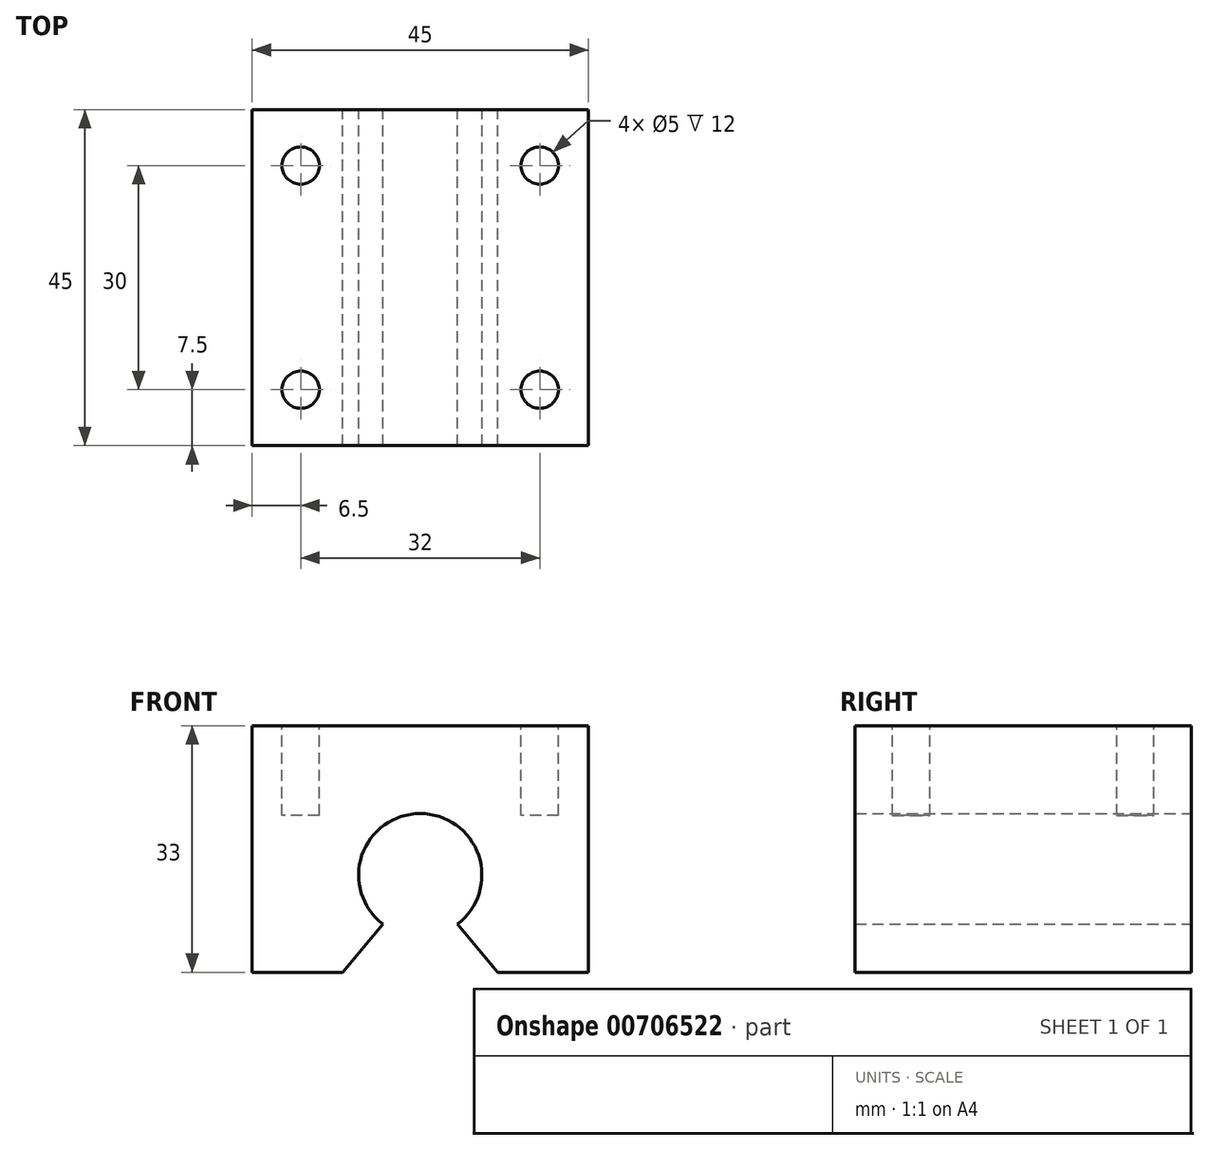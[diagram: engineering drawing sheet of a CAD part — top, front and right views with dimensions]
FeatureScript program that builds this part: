
annotation { "Feature Type Name" : "Feature", "Feature Type Description" : "" }
export const myFeature = defineFeature(function(context is Context, id is Id, definition is map)
    precondition{}
    {
        {
            var Q0;
            Q0=qCreatedBy(makeId("Front.planeOp"),FACE);
            var sketch = newSketch(context, id + "F0", { "sketchPlane" : qUnion([Q0])});
            skLineSegment(sketch, "E0", {"start": v(0, 0) * mm, "end": v(-45, 0) * mm});
            skLineSegment(sketch, "E1", {"start": v(-45, 0) * mm, "end": v(-45, -33) * mm});
            skLineSegment(sketch, "E2", {"start": v(0, 0) * mm, "end": v(0, -33) * mm});
            skArc(sketch, "E3", {"start": v(-17.5, -26.56) * mm, "mid": v(-22.5, -11.75) * mm, "end": v(-27.5, -26.56) * mm});
            skLineSegment(sketch, "E4", {"start": v(-45, -33) * mm, "end": v(-32.9, -33) * mm});
            skLineSegment(sketch, "E5", {"start": v(-32.9, -33) * mm, "end": v(-27.5, -26.56) * mm});
            skLineSegment(sketch, "E6", {"start": v(0, -33) * mm, "end": v(-12.1, -33) * mm});
            skLineSegment(sketch, "E7", {"start": v(-12.1, -33) * mm, "end": v(-17.5, -26.56) * mm});
            skSolve(sketch);
        }
        {
            var Q0;
            Q0 = qSketchRegion(id + "F0", true);
            extrude(context, id + "F1", {"entities" : qUnion([Q0]), "depth" : 45 * mm, "offsetDistance" : 25.4 * mm});
        }
        {
            var Q0;
            Q0=makeQuery(id+"F1.opExtrude","SWEPT_FACE",FACE,{"disambiguationData":[OSD([sQuery(id+"F0.wireOp",EDGE,"E0")])]});
            var sketch = newSketch(context, id + "F2", { "sketchPlane" : qUnion([Q0])});
            skCircle(sketch, "E8", {"center": v(-38.5, -37.5) * mm, "radius": 2.5 * mm});
            skCircle(sketch, "E9", {"center": v(-6.5, -37.5) * mm, "radius": 2.5 * mm});
            skCircle(sketch, "E10", {"center": v(-6.5, -7.5) * mm, "radius": 2.5 * mm});
            skCircle(sketch, "E11", {"center": v(-38.5, -7.5) * mm, "radius": 2.5 * mm});
            skSolve(sketch);
        }
        {
            var Q0;
            Q0 = qSketchRegion(id + "F2", true);
            extrude(context, id + "F3", {"entities" : qUnion([Q0]), "operationType" : NewBodyOperationType.REMOVE, "oppositeDirection" : true, "depth" : 12 * mm, "offsetDistance" : 25.4 * mm});
        }
    });
